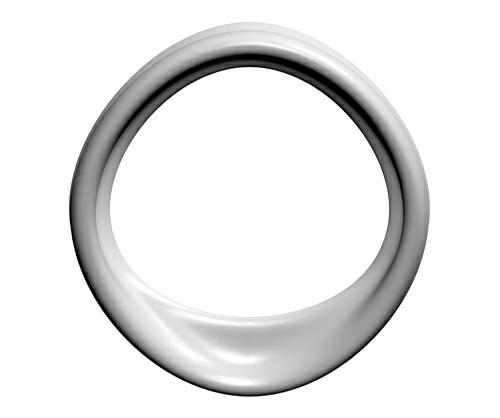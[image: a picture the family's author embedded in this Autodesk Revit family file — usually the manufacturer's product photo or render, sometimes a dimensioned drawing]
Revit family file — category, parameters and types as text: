
# Revit family: CITY ALPHABET letter „O”_vertical
name_source: partatom
category: Furniture
revit_build: Autodesk Revit 2018 (Build: 20190510_1515(x64)
units: mm (PartAtom-declared; Revit-internal decimal feet)

## family parameters
Cut with Voids When Loaded = No
Host = Face
OmniClass Number = 23.40.10.11.14
OmniClass Title = Exterior Seating
Room Calculation Point = No
Shared = No

## types (1)
- CITY ALPHABET letter „O"
    Default Elevation = 1219 mm
    Height = 1900 mm  [stored 6.2336 ft]
    IfcExportAs = IfcFurnishingElement
    Length = 720 mm  [stored 2.3622 ft]
    Manufacturer = Astrini Design
    Material information = Colour choice from RAL colour standard. Customer may inquire about specific request regarding individual order.
    Model = CITY ALPHABET letter „O”
    Operating temperature = -40°C to 80°C, ( -40°F to 176°F )
    Type Comments = Bench
    Type Image = O.jpg
    URL = https://astrini-design.pl
    Weight (approximately) = 60.00 kg
    Weight - filled (approximately) = 110.00 kg
    Width = 1850 mm  [stored 6.06955 ft]

note: [stored X ft] marks values corroborated as IEEE doubles in the binary element streams (Revit-internal decimal feet)
